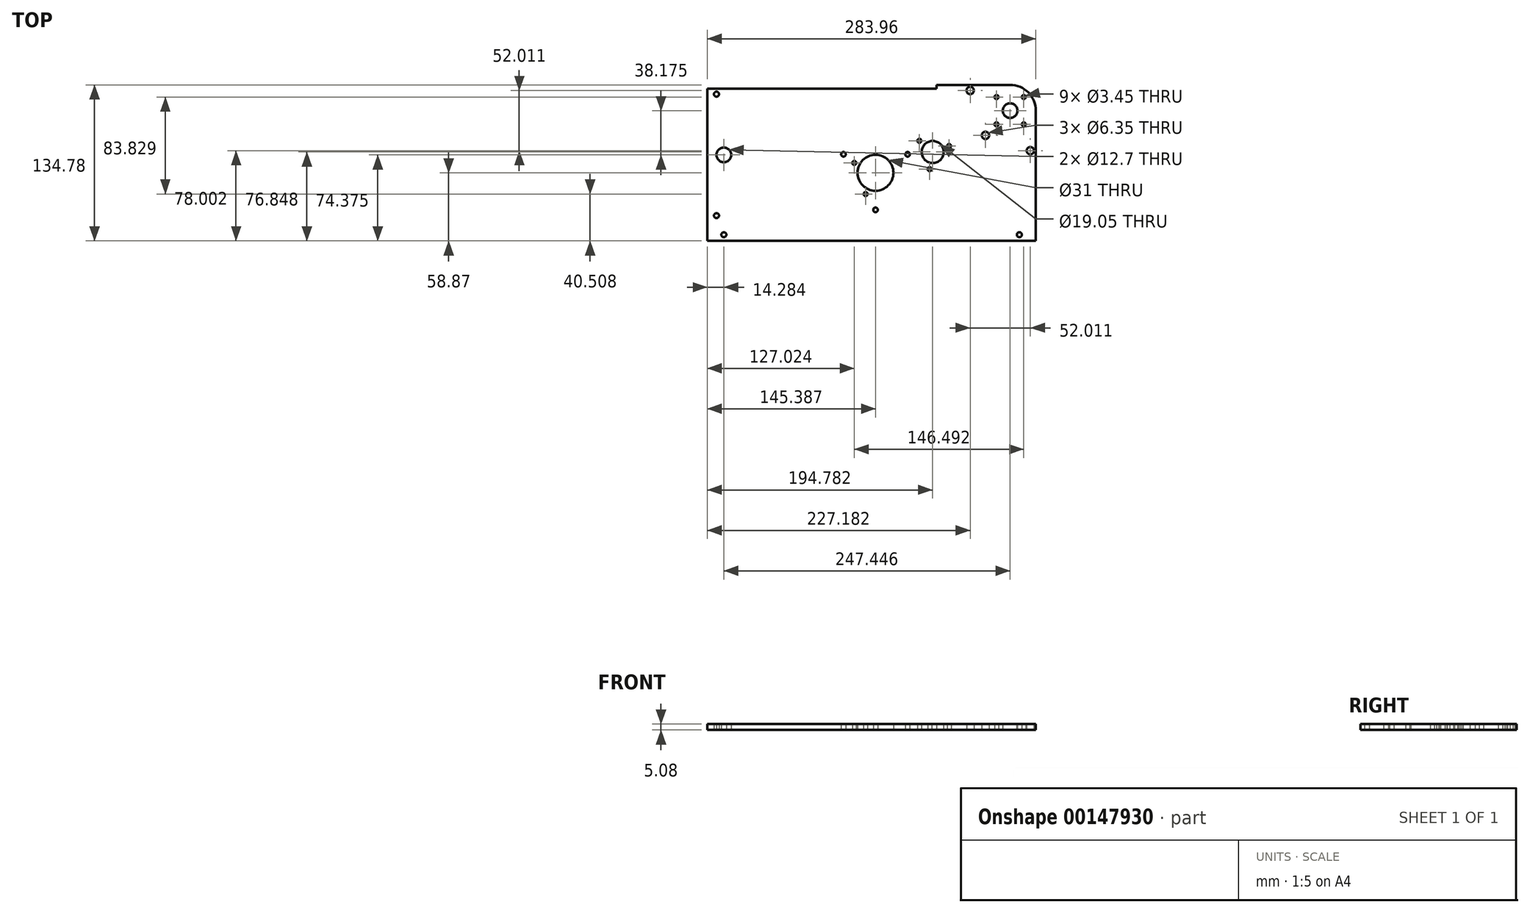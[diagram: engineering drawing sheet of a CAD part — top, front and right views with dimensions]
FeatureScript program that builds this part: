
annotation { "Feature Type Name" : "Feature", "Feature Type Description" : "" }
export const myFeature = defineFeature(function(context is Context, id is Id, definition is map)
    precondition{}
    {
        {
            var Q0;
            Q0=qCreatedBy(makeId("Top.planeOp"),FACE);
            var sketch = newSketch(context, id + "F0", { "sketchPlane" : qUnion([Q0])});
            skCircle(sketch, "E0", {"center": v(0, 0) * mm, "radius": 6.35 * mm});
            skLineSegment(sketch, "E1.top", {"start": v(-261.73, -112.55) * mm, "end": v(22.23, -112.55) * mm});
            skLineSegment(sketch, "E1.left", {"start": v(-261.73, 19.05) * mm, "end": v(-261.73, -112.55) * mm});
            skArc(sketch, "E2", {"start": v(22.23, 0) * mm, "mid": v(15.72, 15.72) * mm, "end": v(0, 22.23) * mm});
            skLineSegment(sketch, "E3", {"start": v(22.23, -112.55) * mm, "end": v(22.23, -101.75) * mm});
            skLineSegment(sketch, "E4", {"start": v(22.23, -101.75) * mm, "end": v(22.23, 0) * mm});
            skLineSegment(sketch, "E5", {"start": v(0, 0) * mm, "end": v(0, -112.55) * mm, "construction": true});
            skLineSegment(sketch, "E6", {"start": v(22.23, -107.15) * mm, "end": v(7.94, -107.15) * mm, "construction": true});
            skCircle(sketch, "E7", {"center": v(7.94, -107.15) * mm, "radius": 2.15 * mm});
            skLineSegment(sketch, "E8", {"start": v(-261.73, -107.15) * mm, "end": v(-247.45, -107.15) * mm, "construction": true});
            skCircle(sketch, "E9", {"center": v(-247.45, -107.15) * mm, "radius": 2.15 * mm});
            skLineSegment(sketch, "E10", {"start": v(-253.8, 19.05) * mm, "end": v(-253.8, 14.29) * mm, "construction": true});
            skLineSegment(sketch, "E11", {"start": v(-253.8, 14.29) * mm, "end": v(-261.73, 14.29) * mm, "construction": true});
            skLineSegment(sketch, "E12", {"start": v(-253.8, 14.29) * mm, "end": v(-253.8, -90.64) * mm, "construction": true});
            skLineSegment(sketch, "E13", {"start": v(-253.8, -90.64) * mm, "end": v(-253.8, -107.15) * mm, "construction": true});
            skCircle(sketch, "E14", {"center": v(-253.8, -90.64) * mm, "radius": 2.15 * mm});
            skCircle(sketch, "E15", {"center": v(-253.8, 14.29) * mm, "radius": 2.15 * mm});
            skCircle(sketch, "E16", {"center": v(-116.34, -53.68) * mm, "radius": 15.5 * mm});
            skCircle(sketch, "E17.cCircle", {"center": v(-116.34, -53.68) * mm, "radius": 16 * mm, "construction": true});
            skLineSegment(sketch, "E17.0", {"start": v(-88.63, -37.68) * mm, "end": v(-116.34, -85.68) * mm, "construction": true});
            skLineSegment(sketch, "E17.1", {"start": v(-116.34, -85.68) * mm, "end": v(-144.06, -37.68) * mm, "construction": true});
            skLineSegment(sketch, "E17.2", {"start": v(-144.06, -37.68) * mm, "end": v(-88.63, -37.68) * mm, "construction": true});
            skCircle(sketch, "E18", {"center": v(-88.63, -37.68) * mm, "radius": 2 * mm});
            skCircle(sketch, "E19", {"center": v(-116.34, -85.68) * mm, "radius": 2 * mm});
            skCircle(sketch, "E20", {"center": v(-144.06, -37.68) * mm, "radius": 2 * mm});
            skLineSegment(sketch, "E21", {"start": v(-116.34, -53.68) * mm, "end": v(-66.95, -35.7) * mm, "construction": true});
            skCircle(sketch, "E22", {"center": v(-66.95, -35.7) * mm, "radius": 9.53 * mm});
            skCircle(sketch, "E23", {"center": v(-66.95, -35.7) * mm, "radius": 11.11 * mm, "construction": true});
            skCircle(sketch, "E24", {"center": v(-52.78, -30.54) * mm, "radius": 3.97 * mm, "construction": true});
            skCircle(sketch, "E25", {"center": v(-69.57, -50.55) * mm, "radius": 1.73 * mm});
            skCircle(sketch, "E26", {"center": v(-78.5, -26) * mm, "radius": 1.73 * mm});
            skCircle(sketch, "E27", {"center": v(-52.78, -30.54) * mm, "radius": 1.73 * mm});
            skCircle(sketch, "E28", {"center": v(-116.34, -53.68) * mm, "radius": 37.5 * mm, "construction": true});
            skCircle(sketch, "E29", {"center": v(-66.95, -35.7) * mm, "radius": 14.29 * mm, "construction": true});
            skLineSegment(sketch, "E30", {"start": v(-66.95, -35.7) * mm, "end": v(0, 0) * mm, "construction": true});
            skLineSegment(sketch, "E31", {"start": v(-116.34, -53.68) * mm, "end": v(-66.95, -53.68) * mm, "construction": true});
            skLineSegment(sketch, "E32", {"start": v(-66.95, -53.68) * mm, "end": v(-66.95, -35.7) * mm, "construction": true});
            skLineSegment(sketch, "E33", {"start": v(-116.34, -53.68) * mm, "end": v(-129.8, -58.58) * mm, "construction": true});
            skLineSegment(sketch, "E34", {"start": v(-134.7, -45.12) * mm, "end": v(-124.9, -72.04) * mm, "construction": true});
            skCircle(sketch, "E35", {"center": v(-134.7, -45.12) * mm, "radius": 4.76 * mm, "construction": true});
            skCircle(sketch, "E36", {"center": v(-134.7, -45.12) * mm, "radius": 1.73 * mm});
            skCircle(sketch, "E37", {"center": v(-124.9, -72.04) * mm, "radius": 1.73 * mm});
            skLineSegment(sketch, "E38", {"start": v(-134.7, -45.12) * mm, "end": v(-116.34, -53.68) * mm, "construction": true});
            skCircle(sketch, "E39", {"center": v(-11.79, 11.79) * mm, "radius": 1.73 * mm});
            skCircle(sketch, "E40", {"center": v(11.79, 11.79) * mm, "radius": 1.73 * mm});
            skCircle(sketch, "E41", {"center": v(-11.79, -11.79) * mm, "radius": 1.73 * mm});
            skLineSegment(sketch, "E42.bottom", {"start": v(11.79, 11.79) * mm, "end": v(-11.79, 11.79) * mm, "construction": true});
            skLineSegment(sketch, "E42.top", {"start": v(11.79, -11.79) * mm, "end": v(-11.79, -11.79) * mm, "construction": true});
            skLineSegment(sketch, "E42.left", {"start": v(11.79, 11.79) * mm, "end": v(11.79, -11.79) * mm, "construction": true});
            skLineSegment(sketch, "E42.right", {"start": v(-11.79, 11.79) * mm, "end": v(-11.79, -11.79) * mm, "construction": true});
            skCircle(sketch, "E43", {"center": v(11.79, -11.79) * mm, "radius": 1.73 * mm});
            skCircle(sketch, "E44", {"center": v(11.79, 11.79) * mm, "radius": 5.56 * mm, "construction": true});
            skLineSegment(sketch, "E45", {"start": v(0, 0) * mm, "end": v(17.46, -34.55) * mm, "construction": true});
            skLineSegment(sketch, "E46", {"start": v(0, 0) * mm, "end": v(-21.33, -21.33) * mm, "construction": true});
            skLineSegment(sketch, "E47", {"start": v(0, 0) * mm, "end": v(-34.55, 17.46) * mm, "construction": true});
            skLineSegment(sketch, "E48", {"start": v(-34.55, 17.46) * mm, "end": v(-21.33, -21.33) * mm, "construction": true});
            skLineSegment(sketch, "E49", {"start": v(17.46, -34.55) * mm, "end": v(-21.33, -21.33) * mm, "construction": true});
            skCircle(sketch, "E50", {"center": v(17.46, -34.55) * mm, "radius": 4.76 * mm, "construction": true});
            skCircle(sketch, "E51", {"center": v(-34.55, 17.46) * mm, "radius": 3.18 * mm});
            skCircle(sketch, "E52", {"center": v(-21.33, -21.33) * mm, "radius": 3.18 * mm});
            skCircle(sketch, "E53", {"center": v(17.46, -34.55) * mm, "radius": 3.18 * mm});
            skLineSegment(sketch, "E54", {"start": v(-116.34, -82.3) * mm, "end": v(-235.9, -82.3) * mm, "construction": true});
            skLineSegment(sketch, "E55", {"start": v(-235.9, -52.9) * mm, "end": v(-235.9, -111.7) * mm, "construction": true});
            skLineSegment(sketch, "E56.bottom", {"start": v(-261.73, 19.05) * mm, "end": v(-63.67, 19.05) * mm});
            skLineSegment(sketch, "E56.right", {"start": v(-63.67, 19.05) * mm, "end": v(-63.67, 22.22) * mm});
            skLineSegment(sketch, "E57", {"start": v(0, 22.23) * mm, "end": v(-63.67, 22.22) * mm});
            skLineSegment(sketch, "E58", {"start": v(-116.34, -53.68) * mm, "end": v(-116.34, -82.3) * mm, "construction": true});
            skLineSegment(sketch, "E59", {"start": v(-253.8, -38.18) * mm, "end": v(-247.45, -38.18) * mm, "construction": true});
            skCircle(sketch, "E60", {"center": v(-247.45, -38.18) * mm, "radius": 6.35 * mm});
            skLineSegment(sketch, "E61", {"start": v(-247.45, -107.15) * mm, "end": v(-235.9, -107.15) * mm, "construction": true});
            skLineSegment(sketch, "E62", {"start": v(-235.9, -82.3) * mm, "end": v(-261.73, -82.3) * mm, "construction": true});
            skCircle(sketch, "E63.cCircle", {"center": v(-66.95, -35.7) * mm, "radius": 7.54 * mm, "construction": true});
            skLineSegment(sketch, "E63.0", {"start": v(-52.78, -30.54) * mm, "end": v(-69.57, -50.55) * mm, "construction": true});
            skLineSegment(sketch, "E63.1", {"start": v(-69.57, -50.55) * mm, "end": v(-78.5, -26) * mm, "construction": true});
            skLineSegment(sketch, "E63.2", {"start": v(-78.5, -26) * mm, "end": v(-52.78, -30.54) * mm, "construction": true});
            skLineSegment(sketch, "E64", {"start": v(-66.95, -35.7) * mm, "end": v(22.23, -35.7) * mm, "construction": true});
            skLineSegment(sketch, "E65", {"start": v(-66.95, -53.68) * mm, "end": v(-66.95, -112.55) * mm, "construction": true});
            skSolve(sketch);
        }
        {
            var Q0;
            Q0=qSketchRegion(id+"F0",true);
            extrude(context, id + "F1", {"entities" : qUnion([Q0]), "depth" : 5.08 * mm});
        }
    });
